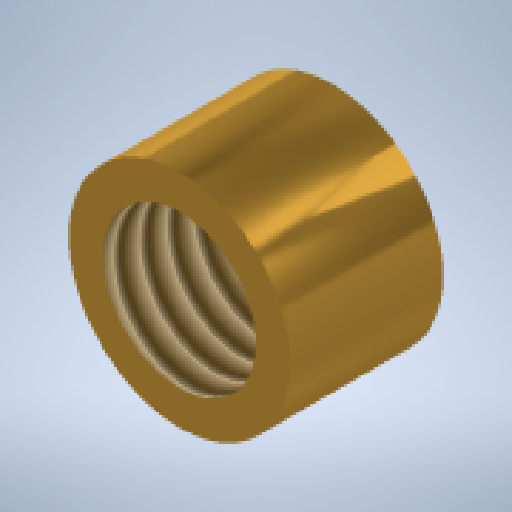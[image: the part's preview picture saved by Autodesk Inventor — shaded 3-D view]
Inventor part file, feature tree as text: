
AUTODESK INVENTOR PART (.ipt)
format: ipt  version: 2024 (Build 280153000, 153)  size: 158,720 bytes
history: native  units: mm
features: other x1, extrude x1, thread x1, sketch x1
ambient origin geometry x8: Origin, YZ Plane, XZ Plane, XY Plane, X Axis, Y Axis, Z Axis, Center Point
bodies: Body1 (feature_tree)
feature tree (4):
  other  "ソリッド1"
  extrude  "押し出し1"  Depth=4.0mm
  thread  "ねじ1"
  sketch  "スケッチ1"
